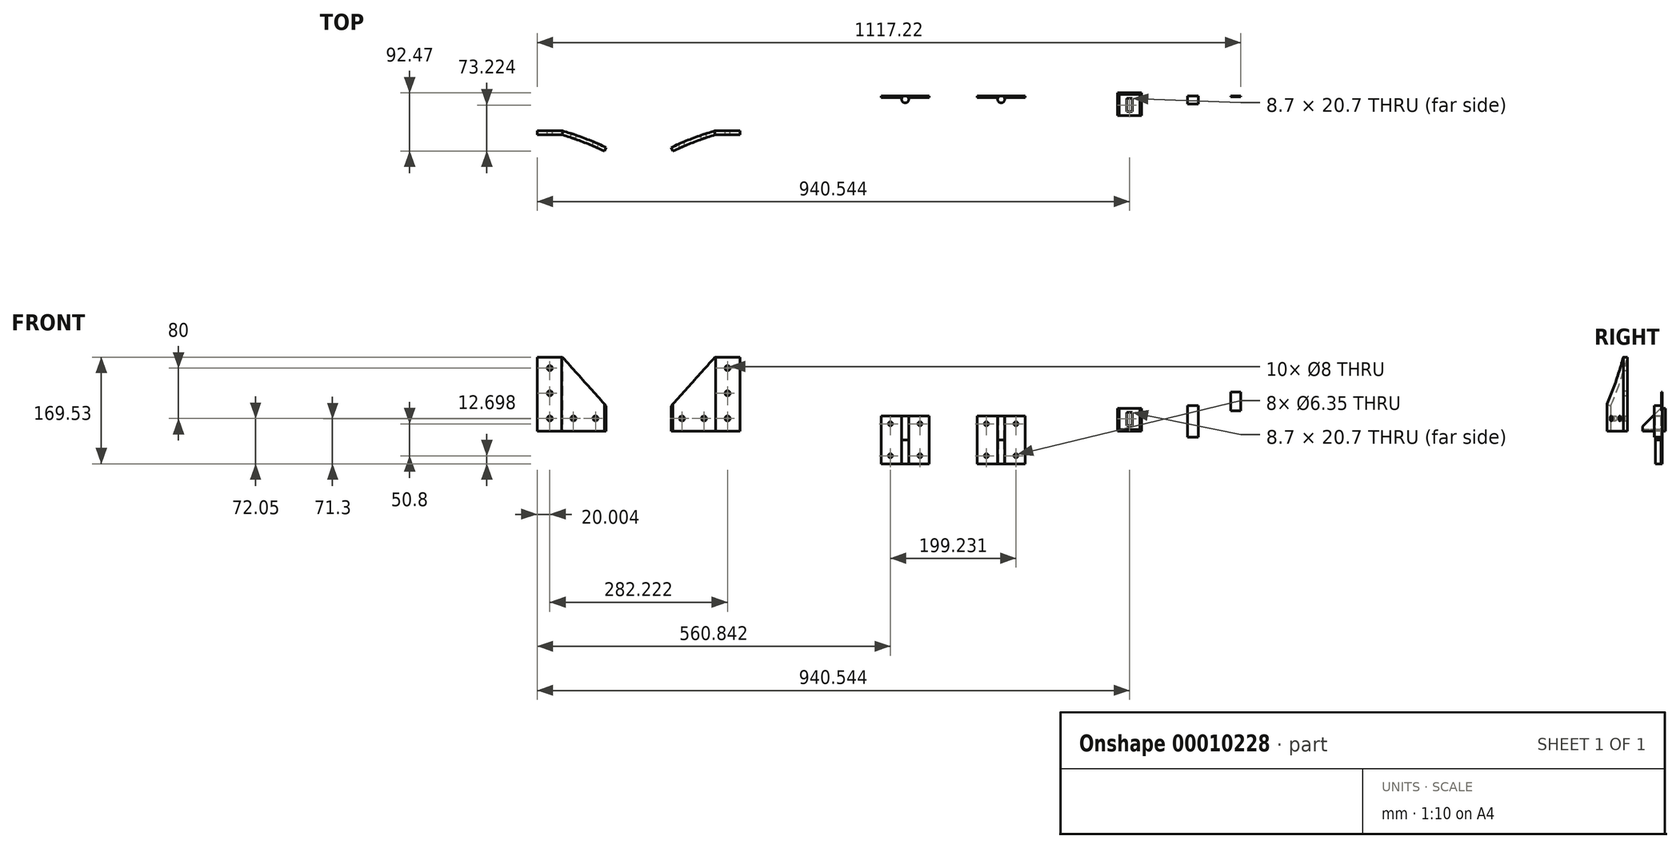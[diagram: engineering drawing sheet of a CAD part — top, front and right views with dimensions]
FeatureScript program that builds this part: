
annotation { "Feature Type Name" : "Feature", "Feature Type Description" : "" }
export const myFeature = defineFeature(function(context is Context, id is Id, definition is map)
    precondition{}
    {
        {
            var Q0;
            Q0=qCreatedBy(makeId("Top.planeOp"),FACE);
            var sketch = newSketch(context, id + "F0", { "sketchPlane" : qUnion([Q0])});
            skLineSegment(sketch, "E0", {"start": v(-288.78, -55.38) * mm, "end": v(-248.78, -55.38) * mm});
            skLineSegment(sketch, "E1", {"start": v(-248.78, -55.38) * mm, "end": v(-380.24, -16.44) * mm});
            skArc(sketch, "E2", {"start": v(-179.38, -81.93) * mm, "mid": v(-213.56, -67.3) * mm, "end": v(-248.78, -55.38) * mm});
            skLineSegment(sketch, "E3", {"start": v(-248.78, -55.38) * mm, "end": v(-385.1, -515.61) * mm, "construction": true});
            skLineSegment(sketch, "E4", {"start": v(-385.1, -515.61) * mm, "end": v(-179.38, -81.93) * mm, "construction": true});
            skArc(sketch, "E5.0", {"start": v(-182.1, -87.67) * mm, "mid": v(-215.4, -73.4) * mm, "end": v(-249.7, -61.73) * mm});
            skLineSegment(sketch, "E5.1", {"start": v(-288.78, -61.73) * mm, "end": v(-249.7, -61.73) * mm});
            skLineSegment(sketch, "E6", {"start": v(-288.78, -61.73) * mm, "end": v(-288.78, -55.38) * mm});
            skLineSegment(sketch, "E7", {"start": v(-182.1, -87.67) * mm, "end": v(-179.38, -81.93) * mm});
            skSolve(sketch);
        }
        {
            var Q0;
            Q0=makeQuery(id+"F0.imprint","IMPRINT",FACE,{"disambiguationData":[TD([[makeQuery(id+"F0.imprint","IMPRINT",EDGE,{"derivedFrom":sQuery(id+"F0.wireOp",EDGE,"E0")}),-1.0]])]});
            extrude(context, id + "F1", {"entities" : qUnion([Q0]), "depth" : 117.47 * mm});
        }
        {
            var Q0;
            Q0=makeQuery(id+"F1.opExtrude","SWEPT_FACE",FACE,{"disambiguationData":[OSD([sQuery(id+"F0.wireOp",EDGE,"E0")])]});
            var sketch = newSketch(context, id + "F2", { "sketchPlane" : qUnion([Q0])});
            skLineSegment(sketch, "E8.0", {"start": v(179.38, 117.48) * mm, "end": v(179.38, 0) * mm});
            skLineSegment(sketch, "E9", {"start": v(248.78, 117.47) * mm, "end": v(179.38, 40) * mm});
            skLineSegment(sketch, "E10", {"start": v(179.38, 0) * mm, "end": v(288.78, 0) * mm});
            skLineSegment(sketch, "E11", {"start": v(288.78, 0) * mm, "end": v(288.78, 117.48) * mm});
            skLineSegment(sketch, "E12", {"start": v(248.78, 117.48) * mm, "end": v(288.78, 117.48) * mm});
            skLineSegment(sketch, "E13", {"start": v(179.38, 40) * mm, "end": v(179.38, 0) * mm});
            skCircle(sketch, "E14", {"center": v(268.78, 100) * mm, "radius": 4 * mm});
            skCircle(sketch, "E15", {"center": v(268.78, 60) * mm, "radius": 4 * mm});
            skCircle(sketch, "E16", {"center": v(268.78, 20) * mm, "radius": 4 * mm});
            skCircle(sketch, "E17", {"center": v(231.28, 20) * mm, "radius": 4 * mm});
            skCircle(sketch, "E18", {"center": v(196.28, 20) * mm, "radius": 4 * mm});
            skPoint(sketch, "E19", {"position": v(268.78, 117.48) * mm});
            skPoint(sketch, "E20", {"position": v(179.38, 20) * mm});
            skLineSegment(sketch, "E21", {"start": v(179.38, 40) * mm, "end": v(179.38, 117.48) * mm});
            skLineSegment(sketch, "E22", {"start": v(179.38, 117.48) * mm, "end": v(248.78, 117.48) * mm});
            skSolve(sketch);
        }
        {
            var Q0;
            Q0=makeQuery(id+"F2.imprint","IMPRINT",FACE,{"disambiguationData":[TD([[makeQuery(id+"F2.imprint","IMPRINT",EDGE,{"derivedFrom":sQuery(id+"F2.wireOp",EDGE,"E18")}),1.0]])]});
            var Q1;
            Q1=makeQuery(id+"F2.imprint","IMPRINT",FACE,{"disambiguationData":[TD([[makeQuery(id+"F2.imprint","IMPRINT",EDGE,{"derivedFrom":sQuery(id+"F2.wireOp",EDGE,"E17")}),1.0]])]});
            var Q2;
            Q2=makeQuery(id+"F2.imprint","IMPRINT",FACE,{"disambiguationData":[TD([[makeQuery(id+"F2.imprint","IMPRINT",EDGE,{"derivedFrom":sQuery(id+"F2.wireOp",EDGE,"E16")}),1.0]])]});
            var Q3;
            Q3=makeQuery(id+"F2.imprint","IMPRINT",FACE,{"disambiguationData":[TD([[makeQuery(id+"F2.imprint","IMPRINT",EDGE,{"derivedFrom":sQuery(id+"F2.wireOp",EDGE,"E15")}),1.0]])]});
            var Q4;
            Q4=makeQuery(id+"F2.imprint","IMPRINT",FACE,{"disambiguationData":[TD([[makeQuery(id+"F2.imprint","IMPRINT",EDGE,{"derivedFrom":sQuery(id+"F2.wireOp",EDGE,"E14")}),1.0]])]});
            var Q5;
            Q5=makeQuery(id+"F2.imprint","IMPRINT",FACE,{"disambiguationData":[TD([[makeQuery(id+"F2.imprint","IMPRINT",EDGE,{"derivedFrom":sQuery(id+"F2.wireOp",EDGE,"E9")}),-1.0]])]});
            extrude(context, id + "F3", {"entities" : qUnion([Q0, Q1, Q2, Q3, Q4, Q5]), "operationType" : NewBodyOperationType.REMOVE, "endBound" : BoundingType.THROUGH_ALL, "oppositeDirection" : true, "depth" : 25 * mm});
        }
        {
            var Q0;
            Q0=makeQuery(id+"F1.opExtrude","SWEPT_BODY",BODY,{"disambiguationData":[OSD([sQuery(id+"F0.wireOp",EDGE,"E0"),sQuery(id+"F0.wireOp",EDGE,"E2"),sQuery(id+"F0.wireOp",EDGE,"E5.0"),sQuery(id+"F0.wireOp",EDGE,"E5.1"),sQuery(id+"F0.wireOp",EDGE,"E6"),sQuery(id+"F0.wireOp",EDGE,"E7")])]});
            transform(context, id + "F4", {"entities" : qUnion([Q0]), "transformType" : TransformType.TRANSLATION_3D, "dx" : 322.22 * mm, "dy" : 0 * mm, "dz" : 0 * mm, "makeCopy" : true});
        }
        {
            var Q0;
            Q0=makeQuery(id+"F4.opPattern","COPY",BODY,{"derivedFrom":makeQuery(id+"F1.opExtrude","SWEPT_BODY",BODY,{"disambiguationData":[OSD([sQuery(id+"F0.wireOp",EDGE,"E0"),sQuery(id+"F0.wireOp",EDGE,"E2"),sQuery(id+"F0.wireOp",EDGE,"E5.0"),sQuery(id+"F0.wireOp",EDGE,"E5.1"),sQuery(id+"F0.wireOp",EDGE,"E6"),sQuery(id+"F0.wireOp",EDGE,"E7")])]}),"instanceName":"1"});
            var Q1;
            Q1=makeQuery(id+"F4.opPattern","COPY",FACE,{"derivedFrom":makeQuery(id+"F1.opExtrude","SWEPT_FACE",FACE,{"disambiguationData":[OSD([sQuery(id+"F0.wireOp",EDGE,"E6")])]}),"instanceName":"1"});
            mirror(context, id + "F5", {"entities" : qUnion([Q0]), "mirrorPlane" : qUnion([Q1])});
        }
        {
            var Q0;
            Q0=makeQuery(id+"F4.opPattern","COPY",BODY,{"derivedFrom":makeQuery(id+"F1.opExtrude","SWEPT_BODY",BODY,{"disambiguationData":[OSD([sQuery(id+"F0.wireOp",EDGE,"E0"),sQuery(id+"F0.wireOp",EDGE,"E2"),sQuery(id+"F0.wireOp",EDGE,"E5.0"),sQuery(id+"F0.wireOp",EDGE,"E5.1"),sQuery(id+"F0.wireOp",EDGE,"E6"),sQuery(id+"F0.wireOp",EDGE,"E7")])]}),"instanceName":"1"});
            deleteBodies(context, id + "F6", {"entities" : qUnion([Q0])});
        }
        {
            var Q0;
            Q0=qCreatedBy(makeId("Front.planeOp"),FACE);
            var sketch = newSketch(context, id + "F7", { "sketchPlane" : qUnion([Q0])});
            skLineSegment(sketch, "E23.bottom", {"start": v(295.48, 24.15) * mm, "end": v(333.58, 24.15) * mm});
            skLineSegment(sketch, "E23.top", {"start": v(295.48, -52.05) * mm, "end": v(333.58, -52.05) * mm});
            skLineSegment(sketch, "E23.left", {"start": v(295.48, 24.15) * mm, "end": v(295.48, -52.05) * mm});
            skLineSegment(sketch, "E23.right", {"start": v(333.58, 24.15) * mm, "end": v(333.58, -52.05) * mm});
            skCircle(sketch, "E24", {"center": v(318.9, 11.45) * mm, "radius": 3.18 * mm});
            skCircle(sketch, "E25", {"center": v(318.9, -39.35) * mm, "radius": 3.18 * mm});
            skSolve(sketch);
        }
        {
            var Q0;
            Q0=makeQuery(id+"F7.imprint","IMPRINT",FACE,{"disambiguationData":[TD([[makeQuery(id+"F7.imprint","IMPRINT",EDGE,{"derivedFrom":sQuery(id+"F7.wireOp",EDGE,"E23.bottom")}),-1.0]])]});
            extrude(context, id + "F8", {"entities" : qUnion([Q0]), "depth" : 2.36 * mm});
        }
        {
            var Q0;
            Q0=makeQuery(id+"F8.opExtrude","SWEPT_FACE",FACE,{"disambiguationData":[OSD([sQuery(id+"F7.wireOp",EDGE,"E23.top")])]});
            var sketch = newSketch(context, id + "F9", { "sketchPlane" : qUnion([Q0])});
            skCircle(sketch, "E26", {"center": v(295.48, 5.56) * mm, "radius": 5.56 * mm});
            skSolve(sketch);
        }
        {
            var Q0;
            {var subQ0=sQuery(id+"F7.wireOp",EDGE,"E23.top");var subQ4=makeQuery(id+"F8.opExtrude","SWEPT_EDGE",EDGE,{"disambiguationData":[OSD([subQ0,sQuery(id+"F7.wireOp",EDGE,"E23.left")])]});Q0=makeQuery(id+"F9.imprint","IMPRINT",FACE,{"disambiguationData":[TD([[makeQuery(id+"F9.imprint","IMPRINT",EDGE,{"derivedFrom":subQ4}),-1.0]])]});}
            extrude(context, id + "F10", {"entities" : qUnion([Q0]), "operationType" : NewBodyOperationType.ADD, "oppositeDirection" : true, "depth" : 38.1 * mm});
        }
        {
            var Q0;
            Q0=makeQuery(id+"F10.opExtrude","CAP_FACE",FACE,{"disambiguationData":[OSD([sQuery(id+"F7.wireOp",EDGE,"E23.top"),sQuery(id+"F7.wireOp",EDGE,"E23.left"),sQuery(id+"F9.wireOp",EDGE,"E26")])],"isStart":false});
            var sketch = newSketch(context, id + "F11", { "sketchPlane" : qUnion([Q0])});
            skArc(sketch, "E27.0", {"start": v(300.02, -2.36) * mm, "mid": v(292.92, -10.49) * mm, "end": v(295.48, 0) * mm});
            skArc(sketch, "E28", {"start": v(300.02, -2.36) * mm, "mid": v(298.04, -0.63) * mm, "end": v(295.48, 0) * mm});
            skLineSegment(sketch, "E29", {"start": v(295.48, 0) * mm, "end": v(300.02, 0) * mm});
            skLineSegment(sketch, "E30", {"start": v(300.02, 0) * mm, "end": v(300.02, -2.36) * mm});
            skSolve(sketch);
        }
        {
            var Q0;
            Q0=makeQuery(id+"F11.imprint","IMPRINT",FACE,{"disambiguationData":[TD([[makeQuery(id+"F11.imprint","IMPRINT",EDGE,{"derivedFrom":sQuery(id+"F11.wireOp",EDGE,"E28")}),1.0]])]});
            var Q1;
            Q1=makeQuery(id+"F11.imprint","IMPRINT",FACE,{"disambiguationData":[TD([[makeQuery(id+"F11.imprint","IMPRINT",EDGE,{"derivedFrom":sQuery(id+"F11.wireOp",EDGE,"E28")}),-1.0]])]});
            extrude(context, id + "F12", {"entities" : qUnion([Q0, Q1]), "operationType" : NewBodyOperationType.REMOVE, "endBound" : BoundingType.UP_TO_NEXT, "depth" : 25 * mm});
        }
        {
            var Q0;
            Q0=makeQuery(id+"F8.opExtrude","SWEPT_BODY",BODY,{"disambiguationData":[OSD([sQuery(id+"F7.wireOp",EDGE,"E23.bottom"),sQuery(id+"F7.wireOp",EDGE,"E23.top"),sQuery(id+"F7.wireOp",EDGE,"E23.left"),sQuery(id+"F7.wireOp",EDGE,"E23.right"),sQuery(id+"F7.wireOp",EDGE,"E24"),sQuery(id+"F7.wireOp",EDGE,"E25")])]});
            var Q1;
            Q1=makeQuery(id+"F8.opExtrude","SWEPT_EDGE",EDGE,{"disambiguationData":[OSD([sQuery(id+"F7.wireOp",EDGE,"E23.top"),sQuery(id+"F7.wireOp",EDGE,"E23.right")])]});
            transform(context, id + "F13", {"entities" : qUnion([Q0]), "transformType" : TransformType.ROTATION, "transformAxis" : qUnion([Q1]), "angle" : 180 * degree, "makeCopy" : true});
        }
        {
            var Q0;
            Q0=makeQuery(id+"F13.opPattern","COPY",BODY,{"derivedFrom":makeQuery(id+"F8.opExtrude","SWEPT_BODY",BODY,{"disambiguationData":[OSD([sQuery(id+"F7.wireOp",EDGE,"E23.bottom"),sQuery(id+"F7.wireOp",EDGE,"E23.top"),sQuery(id+"F7.wireOp",EDGE,"E23.left"),sQuery(id+"F7.wireOp",EDGE,"E23.right"),sQuery(id+"F7.wireOp",EDGE,"E24"),sQuery(id+"F7.wireOp",EDGE,"E25")])]}),"instanceName":"1"});
            transform(context, id + "F14", {"entities" : qUnion([Q0]), "transformType" : TransformType.TRANSLATION_3D, "dx" : -76.2 * mm, "dy" : 0 * mm, "dz" : 76.2 * mm, "makeCopy" : false});
        }
        {
            var Q0;
            Q0=makeQuery(id+"F8.opExtrude","SWEPT_BODY",BODY,{"disambiguationData":[OSD([sQuery(id+"F7.wireOp",EDGE,"E23.bottom"),sQuery(id+"F7.wireOp",EDGE,"E23.top"),sQuery(id+"F7.wireOp",EDGE,"E23.left"),sQuery(id+"F7.wireOp",EDGE,"E23.right"),sQuery(id+"F7.wireOp",EDGE,"E24"),sQuery(id+"F7.wireOp",EDGE,"E25")])]});
            transform(context, id + "F15", {"entities" : qUnion([Q0]), "transformType" : TransformType.TRANSLATION_3D, "dx" : 228.6 * mm, "dy" : 0 * mm, "dz" : 0 * mm, "makeCopy" : true});
        }
        {
            var Q0;
            Q0=makeQuery(id+"F13.opPattern","COPY",BODY,{"derivedFrom":makeQuery(id+"F8.opExtrude","SWEPT_BODY",BODY,{"disambiguationData":[OSD([sQuery(id+"F7.wireOp",EDGE,"E23.bottom"),sQuery(id+"F7.wireOp",EDGE,"E23.top"),sQuery(id+"F7.wireOp",EDGE,"E23.left"),sQuery(id+"F7.wireOp",EDGE,"E23.right"),sQuery(id+"F7.wireOp",EDGE,"E24"),sQuery(id+"F7.wireOp",EDGE,"E25")])]}),"instanceName":"1"});
            transform(context, id + "F16", {"entities" : qUnion([Q0]), "transformType" : TransformType.TRANSLATION_3D, "dx" : 228.6 * mm, "dy" : 0 * mm, "dz" : 0 * mm, "makeCopy" : true});
        }
        {
            var Q0;
            Q0=makeQuery(id+"F16.opPattern","COPY",BODY,{"derivedFrom":makeQuery(id+"F13.opPattern","COPY",BODY,{"derivedFrom":makeQuery(id+"F8.opExtrude","SWEPT_BODY",BODY,{"disambiguationData":[OSD([sQuery(id+"F7.wireOp",EDGE,"E23.bottom"),sQuery(id+"F7.wireOp",EDGE,"E23.top"),sQuery(id+"F7.wireOp",EDGE,"E23.left"),sQuery(id+"F7.wireOp",EDGE,"E23.right"),sQuery(id+"F7.wireOp",EDGE,"E24"),sQuery(id+"F7.wireOp",EDGE,"E25")])]}),"instanceName":"1"}),"instanceName":"1"});
            var Q1;
            Q1=makeQuery(id+"F15.opPattern","COPY",BODY,{"derivedFrom":makeQuery(id+"F8.opExtrude","SWEPT_BODY",BODY,{"disambiguationData":[OSD([sQuery(id+"F7.wireOp",EDGE,"E23.bottom"),sQuery(id+"F7.wireOp",EDGE,"E23.top"),sQuery(id+"F7.wireOp",EDGE,"E23.left"),sQuery(id+"F7.wireOp",EDGE,"E23.right"),sQuery(id+"F7.wireOp",EDGE,"E24"),sQuery(id+"F7.wireOp",EDGE,"E25")])]}),"instanceName":"1"});
            var Q2;
            Q2=makeQuery(id+"F16.opPattern","COPY",FACE,{"derivedFrom":makeQuery(id+"F13.opPattern","COPY",FACE,{"derivedFrom":makeQuery(id+"F8.opExtrude","SWEPT_FACE",FACE,{"disambiguationData":[OSD([sQuery(id+"F7.wireOp",EDGE,"E23.right")])]}),"instanceName":"1"}),"instanceName":"1"});
            mirror(context, id + "F17", {"entities" : qUnion([Q0, Q1]), "mirrorPlane" : qUnion([Q2])});
        }
        {
            var Q0;
            Q0=makeQuery(id+"F15.opPattern","COPY",BODY,{"derivedFrom":makeQuery(id+"F8.opExtrude","SWEPT_BODY",BODY,{"disambiguationData":[OSD([sQuery(id+"F7.wireOp",EDGE,"E23.bottom"),sQuery(id+"F7.wireOp",EDGE,"E23.top"),sQuery(id+"F7.wireOp",EDGE,"E23.left"),sQuery(id+"F7.wireOp",EDGE,"E23.right"),sQuery(id+"F7.wireOp",EDGE,"E24"),sQuery(id+"F7.wireOp",EDGE,"E25")])]}),"instanceName":"1"});
            var Q1;
            Q1=makeQuery(id+"F16.opPattern","COPY",BODY,{"derivedFrom":makeQuery(id+"F13.opPattern","COPY",BODY,{"derivedFrom":makeQuery(id+"F8.opExtrude","SWEPT_BODY",BODY,{"disambiguationData":[OSD([sQuery(id+"F7.wireOp",EDGE,"E23.bottom"),sQuery(id+"F7.wireOp",EDGE,"E23.top"),sQuery(id+"F7.wireOp",EDGE,"E23.left"),sQuery(id+"F7.wireOp",EDGE,"E23.right"),sQuery(id+"F7.wireOp",EDGE,"E24"),sQuery(id+"F7.wireOp",EDGE,"E25")])]}),"instanceName":"1"}),"instanceName":"1"});
            deleteBodies(context, id + "F18", {"entities" : qUnion([Q0, Q1])});
        }
        {
            var Q0;
            Q0=qCreatedBy(makeId("Top.planeOp"),FACE);
            var sketch = newSketch(context, id + "F19", { "sketchPlane" : qUnion([Q0])});
            skLineSegment(sketch, "E31.bottom", {"start": v(632.76, 4.8) * mm, "end": v(670.76, 4.8) * mm});
            skLineSegment(sketch, "E31.top", {"start": v(632.76, -31.2) * mm, "end": v(670.76, -31.2) * mm});
            skLineSegment(sketch, "E31.left", {"start": v(632.76, 4.8) * mm, "end": v(632.76, -31.2) * mm});
            skLineSegment(sketch, "E31.right", {"start": v(670.76, 4.8) * mm, "end": v(670.76, -31.2) * mm});
            skLineSegment(sketch, "E32.bottom", {"start": v(647.41, -4.1) * mm, "end": v(656.11, -4.1) * mm});
            skLineSegment(sketch, "E32.top", {"start": v(647.41, -24.8) * mm, "end": v(656.11, -24.8) * mm});
            skLineSegment(sketch, "E32.left", {"start": v(647.41, -4.1) * mm, "end": v(647.41, -24.8) * mm});
            skLineSegment(sketch, "E32.right", {"start": v(656.11, -4.1) * mm, "end": v(656.11, -24.8) * mm});
            skPoint(sketch, "E33", {"position": v(651.76, -31.2) * mm});
            skPoint(sketch, "E34", {"position": v(651.76, -24.8) * mm});
            skPoint(sketch, "E35", {"position": v(647.41, -14.45) * mm});
            skLineSegment(sketch, "E36", {"start": v(632.76, -31.2) * mm, "end": v(632.76, 2.3) * mm, "construction": true});
            skPoint(sketch, "E37", {"position": v(632.76, -14.45) * mm});
            skSolve(sketch);
        }
        {
            var Q0;
            Q0=makeQuery(id+"F19.imprint","IMPRINT",FACE,{"disambiguationData":[TD([[makeQuery(id+"F19.imprint","IMPRINT",EDGE,{"derivedFrom":sQuery(id+"F19.wireOp",EDGE,"E31.bottom")}),-1.0]])]});
            extrude(context, id + "F20", {"entities" : qUnion([Q0]), "depth" : 2.5 * mm});
        }
        {
            var Q0;
            Q0=makeQuery(id+"F20.opExtrude","SWEPT_FACE",FACE,{"disambiguationData":[OSD([sQuery(id+"F19.wireOp",EDGE,"E31.bottom")])]});
            var sketch = newSketch(context, id + "F21", { "sketchPlane" : qUnion([Q0])});
            skLineSegment(sketch, "E38.bottom", {"start": v(-670.76, 0) * mm, "end": v(-632.76, 0) * mm});
            skLineSegment(sketch, "E38.top", {"start": v(-670.76, 36) * mm, "end": v(-632.76, 36) * mm});
            skLineSegment(sketch, "E38.left", {"start": v(-670.76, 0) * mm, "end": v(-670.76, 36) * mm});
            skLineSegment(sketch, "E38.right", {"start": v(-632.76, 0) * mm, "end": v(-632.76, 36) * mm});
            skLineSegment(sketch, "E39.bottom", {"start": v(-647.41, 29.6) * mm, "end": v(-656.11, 29.6) * mm});
            skLineSegment(sketch, "E39.top", {"start": v(-647.41, 8.9) * mm, "end": v(-656.11, 8.9) * mm});
            skLineSegment(sketch, "E39.left", {"start": v(-647.41, 29.6) * mm, "end": v(-647.41, 8.9) * mm});
            skLineSegment(sketch, "E39.right", {"start": v(-656.11, 29.6) * mm, "end": v(-656.11, 8.9) * mm});
            skLineSegment(sketch, "E40", {"start": v(-632.76, 36) * mm, "end": v(-632.76, 2.5) * mm, "construction": true});
            skPoint(sketch, "E41", {"position": v(-632.76, 19.25) * mm});
            skPoint(sketch, "E42", {"position": v(-647.41, 19.25) * mm});
            skPoint(sketch, "E43", {"position": v(-651.76, 29.6) * mm});
            skPoint(sketch, "E44", {"position": v(-651.76, 36) * mm});
            skSolve(sketch);
        }
        {
            var Q0;
            {var subQ2=sQuery(id+"F21.wireOp",EDGE,"E38.top");Q0=makeQuery(id+"F21.imprint","IMPRINT",FACE,{"disambiguationData":[TD([[makeQuery(id+"F21.imprint","IMPRINT",EDGE,{"derivedFrom":subQ2}),-1.0]])]});}
            extrude(context, id + "F22", {"entities" : qUnion([Q0]), "operationType" : NewBodyOperationType.ADD, "oppositeDirection" : true, "depth" : 2.5 * mm});
        }
        {
            var Q0;
            Q0=makeQuery(id+"F22.boolean.opBoolean","MERGE",FACE,{"derivedFrom":[makeQuery(id+"F20.opExtrude","SWEPT_FACE",FACE,{"disambiguationData":[OSD([sQuery(id+"F19.wireOp",EDGE,"E31.right")])]}),makeQuery(id+"F22.opExtrude","SWEPT_FACE",FACE,{"disambiguationData":[OSD([sQuery(id+"F21.wireOp",EDGE,"E38.left")])]})]});
            var sketch = newSketch(context, id + "F23", { "sketchPlane" : qUnion([Q0])});
            skLineSegment(sketch, "E45", {"start": v(-31.2, 2.5) * mm, "end": v(-31.2, 7.5) * mm});
            skLineSegment(sketch, "E46", {"start": v(-31.2, 7.5) * mm, "end": v(-2.7, 36) * mm});
            skLineSegment(sketch, "E47", {"start": v(-2.7, 36) * mm, "end": v(2.3, 36) * mm});
            skSolve(sketch);
        }
        {
            var Q0;
            Q0=makeQuery(id+"F23.imprint","IMPRINT",FACE,{"disambiguationData":[TD([[makeQuery(id+"F23.imprint","IMPRINT",EDGE,{"derivedFrom":sQuery(id+"F23.wireOp",EDGE,"E45")}),-1.0]])]});
            extrude(context, id + "F24", {"entities" : qUnion([Q0]), "operationType" : NewBodyOperationType.ADD, "oppositeDirection" : true, "depth" : 2.5 * mm});
        }
        {
            var Q0;
            Q0=makeQuery(id+"F22.boolean.opBoolean","MERGE",FACE,{"derivedFrom":[makeQuery(id+"F20.opExtrude","SWEPT_FACE",FACE,{"disambiguationData":[OSD([sQuery(id+"F19.wireOp",EDGE,"E31.left")])]}),makeQuery(id+"F22.opExtrude","SWEPT_FACE",FACE,{"disambiguationData":[OSD([sQuery(id+"F21.wireOp",EDGE,"E38.right")])]})]});
            var sketch = newSketch(context, id + "F25", { "sketchPlane" : qUnion([Q0])});
            skLineSegment(sketch, "E48.0.0", {"start": v(31.2, 2.5) * mm, "end": v(31.2, 7.5) * mm});
            skLineSegment(sketch, "E48.0.1", {"start": v(31.2, 7.5) * mm, "end": v(2.7, 36) * mm});
            skLineSegment(sketch, "E48.0.2", {"start": v(2.7, 36) * mm, "end": v(-2.3, 36) * mm});
            skLineSegment(sketch, "E48.0.3", {"start": v(-2.3, 36) * mm, "end": v(-2.3, 2.5) * mm});
            skLineSegment(sketch, "E48.0.4", {"start": v(-2.3, 2.5) * mm, "end": v(31.2, 2.5) * mm});
            skSolve(sketch);
        }
        {
            var Q0;
            Q0=makeQuery(id+"F25.imprint","IMPRINT",FACE,{"disambiguationData":[TD([[makeQuery(id+"F25.imprint","IMPRINT",EDGE,{"derivedFrom":sQuery(id+"F25.wireOp",EDGE,"E48.0.0")}),1.0]])]});
            extrude(context, id + "F26", {"entities" : qUnion([Q0]), "operationType" : NewBodyOperationType.ADD, "oppositeDirection" : true, "depth" : 2.5 * mm});
        }
        {
            var Q0;
            Q0=qCreatedBy(makeId("Front.planeOp"),FACE);
            var sketch = newSketch(context, id + "F27", { "sketchPlane" : qUnion([Q0])});
            skLineSegment(sketch, "E49.bottom", {"start": v(760.76, -9.85) * mm, "end": v(743.76, -9.85) * mm});
            skLineSegment(sketch, "E49.top", {"start": v(760.76, 40.15) * mm, "end": v(743.76, 40.15) * mm});
            skLineSegment(sketch, "E49.left", {"start": v(760.76, -9.85) * mm, "end": v(760.76, 40.15) * mm});
            skLineSegment(sketch, "E49.right", {"start": v(743.76, -9.85) * mm, "end": v(743.76, 40.15) * mm});
            skSolve(sketch);
        }
        {
            var Q0;
            Q0=makeQuery(id+"F27.imprint","IMPRINT",FACE,{"disambiguationData":[TD([[makeQuery(id+"F27.imprint","IMPRINT",EDGE,{"derivedFrom":sQuery(id+"F27.wireOp",EDGE,"E49.bottom")}),-1.0]])]});
            extrude(context, id + "F28", {"entities" : qUnion([Q0]), "depth" : 13 * mm});
        }
        {
            var Q0;
            Q0=qCreatedBy(makeId("Front.planeOp"),FACE);
            var sketch = newSketch(context, id + "F29", { "sketchPlane" : qUnion([Q0])});
            skLineSegment(sketch, "E50.bottom", {"start": v(812.44, 31.88) * mm, "end": v(828.44, 31.88) * mm});
            skLineSegment(sketch, "E50.top", {"start": v(812.44, 61.88) * mm, "end": v(828.44, 61.88) * mm});
            skLineSegment(sketch, "E50.left", {"start": v(812.44, 61.88) * mm, "end": v(812.44, 31.88) * mm});
            skLineSegment(sketch, "E50.right", {"start": v(828.44, 61.88) * mm, "end": v(828.44, 31.88) * mm});
            skSolve(sketch);
        }
        {
            var Q0;
            Q0=makeQuery(id+"F29.imprint","IMPRINT",FACE,{"disambiguationData":[TD([[makeQuery(id+"F29.imprint","IMPRINT",EDGE,{"derivedFrom":sQuery(id+"F29.wireOp",EDGE,"E50.bottom")}),1.0]])]});
            extrude(context, id + "F30", {"entities" : qUnion([Q0]), "depth" : 1.6 * mm});
        }
    });
